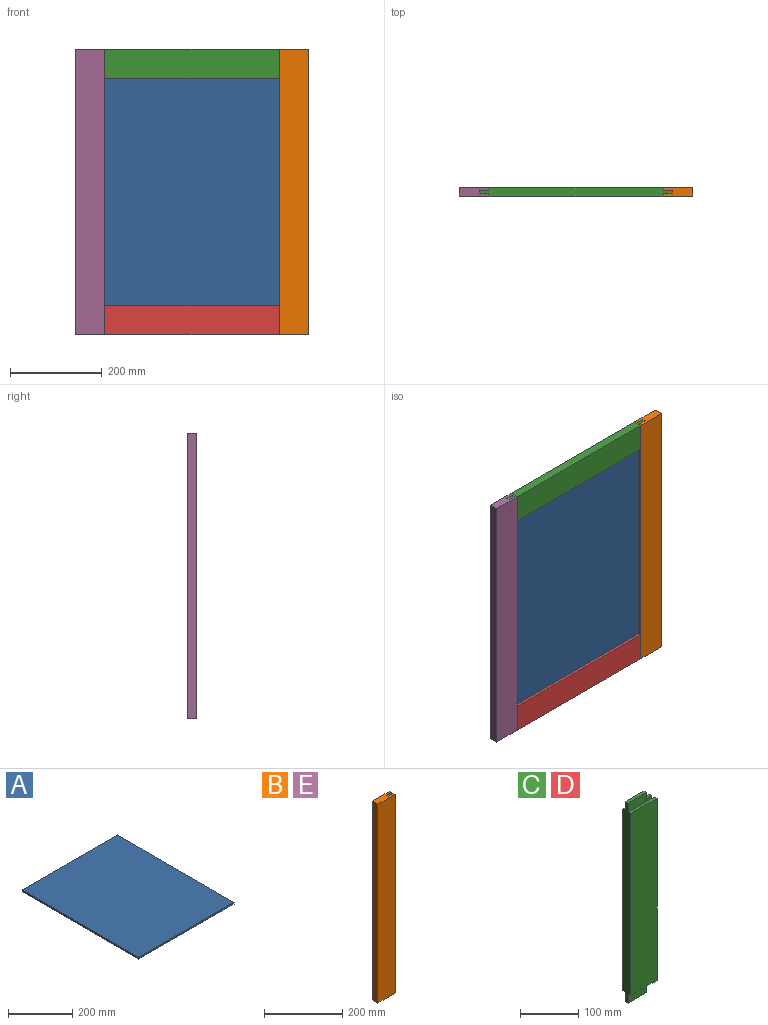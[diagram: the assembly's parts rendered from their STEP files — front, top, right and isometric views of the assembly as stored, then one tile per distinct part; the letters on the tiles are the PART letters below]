
ASSEMBLY  parts=5 mates=4
PART A: 6 faces, bbox 419.1x514.4x6.4 mm
  f0: plane 514.35x6.35mm, normal (-1,0,0), area 3266.1mm2, adj f1,f3,f4,f5
  f1: plane 419.1x6.35mm, normal (0,-1,0), area 2661.3mm2, adj f0,f2,f4,f5
  f2: plane 514.35x6.35mm, normal (1,0,0), area 3266.1mm2, adj f1,f3,f4,f5
  f3: plane 419.1x6.35mm, normal (0,1,0), area 2661.3mm2, adj f0,f2,f4,f5
  f4: plane 514.35x419.1mm, normal (0,0,1), area 215564.1mm2, adj f0,f1,f2,f3
  f5: plane 514.35x419.1mm, normal (0,0,-1), area 215564.1mm2, adj f0,f1,f2,f3
PART B: 10 faces, bbox 63.5x19.1x622.3 mm
  f0: plane 622.3x6.35mm, normal (1,0,0), area 3951.6mm2, adj f1,f3,f6,f7
  f1: plane 63.5x19.05mm, normal (0,0,-1), area 1088.7mm2, adj f0,f2,f3,f4,f5,f7,f8,f9
  f2: plane 622.3x19.05mm, normal (-1,0,0), area 11854.8mm2, adj f1,f3,f5,f6
  f3: plane 622.3x63.5mm, normal (0,-1,0), area 39516mm2, adj f0,f1,f2,f6
  f4: plane 622.3x6.35mm, normal (1,0,0), area 3951.6mm2, adj f1,f5,f6,f9
  f5: plane 622.3x63.5mm, normal (0,1,0), area 39516mm2, adj f1,f2,f4,f6
  f6: plane 63.5x19.05mm, normal (0,0,1), area 1088.7mm2, adj f0,f2,f3,f4,f5,f7,f8,f9
  f7: plane 622.3x19.05mm, normal (0,1,0), area 11854.8mm2, adj f0,f1,f6,f8
  f8: plane 622.3x6.35mm, normal (1,0,0), area 3951.6mm2, adj f1,f6,f7,f9
  f9: plane 622.3x19.05mm, normal (0,-1,0), area 11854.8mm2, adj f1,f4,f6,f8
PART C: 18 faces, bbox 63.5x19.1x419.1 mm
  f0: plane 44.45x6.35mm, normal (0,0,1), area 282.3mm2, adj f1,f9,f12,f16
  f1: plane 419.1x19.05mm, normal (-1,0,0), area 7500mm2, adj f0,f2,f3,f4,f10,f11,f12,f13
  f2: plane 381x63.5mm, normal (0,-1,0), area 24193.5mm2, adj f1,f7,f14,f17
  f3: plane 381x63.5mm, normal (0,1,0), area 24193.5mm2, adj f1,f8,f10,f13
  f4: plane 44.45x6.35mm, normal (0,0,-1), area 282.3mm2, adj f1,f9,f11,f15
  f5: plane 381x19.05mm, normal (0,-1,0), area 7258.1mm2, adj f8,f9,f10,f13
  f6: plane 381x19.05mm, normal (0,1,0), area 7258.1mm2, adj f7,f9,f14,f17
  f7: plane 381x6.35mm, normal (1,0,0), area 2419.3mm2, adj f2,f6,f14,f17
  f8: plane 381x6.35mm, normal (1,0,0), area 2419.4mm2, adj f3,f5,f10,f13
  f9: plane 419.1x6.35mm, normal (1,0,0), area 2661.3mm2, adj f0,f4,f5,f6,f11,f12,f15,f16
  f10: plane 63.5x6.35mm, normal (0,0,-1), area 403.2mm2, adj f1,f3,f5,f8,f11
  f11: plane 44.45x19.05mm, normal (0,1,0), area 846.8mm2, adj f1,f4,f9,f10
  f12: plane 44.45x19.05mm, normal (0,1,0), area 846.8mm2, adj f0,f1,f9,f13
  f13: plane 63.5x6.35mm, normal (0,0,1), area 403.2mm2, adj f1,f3,f5,f8,f12
  f14: plane 63.5x6.35mm, normal (0,0,-1), area 403.2mm2, adj f1,f2,f6,f7,f15
  f15: plane 44.45x19.05mm, normal (0,-1,0), area 846.8mm2, adj f1,f4,f9,f14
  f16: plane 44.45x19.05mm, normal (0,-1,0), area 846.8mm2, adj f0,f1,f9,f17
  f17: plane 63.5x6.35mm, normal (0,0,1), area 403.2mm2, adj f1,f2,f6,f7,f16
PART D: same geometry as C
PART E: same geometry as B
PLACE A rot(axis=(1,0,0),90deg) t=(44.45,12.7,53.98)mm
PLACE B rot(axis=(0,0,1),180deg) t=(508,19.05,0)mm
PLACE C rot(axis=(0.71,0,-0.71),180deg) t=(463.55,19.05,622.3)mm
PLACE D rot(axis=(0,-1,0),90deg) t=(463.55,0,0)mm
PLACE E at identity
MATE fastened C.f17 <-> E.f4  axis (-1,0,0) through (63.5,19.05,622.3)mm
MATE fastened B.f0 <-> C.f14  axis (-1,0,0) through (444.5,19.05,622.3)mm
MATE fastened D.f17 <-> E.f0  axis (-1,0,0) through (63.5,0,0)mm
MATE fastened A.f0 <-> E.f8  axis (-1,0,0) through (44.45,9.53,311.15)mm
